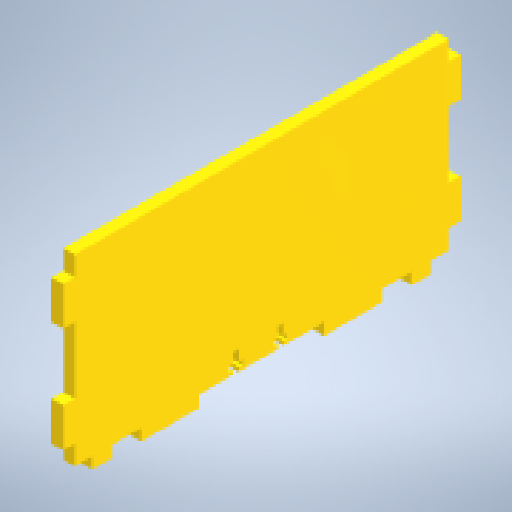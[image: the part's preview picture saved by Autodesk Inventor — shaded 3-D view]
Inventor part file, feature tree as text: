
AUTODESK INVENTOR PART (.ipt)
format: ipt  version: 2024.2 (Build 282272000, 272)  size: 230,912 bytes
history: native  units: mm
features: extrude x3, sketch x3, other x1
ambient origin geometry x8: Origin, YZ Plane, XZ Plane, XY Plane, X Axis, Y Axis, Z Axis, Center Point
bodies: Body1 (feature_tree)
feature tree (7):
  other  "Твердое тело1"
  extrude  "Выдавливание1"  Depth=204.0mm
  extrude  "Выдавливание2"  Depth=100.0mm
  extrude  "Выдавливание4"  Depth=40.0mm
  sketch  "Эскиз1"
  sketch  "Эскиз2"
  sketch  "Эскиз4"
